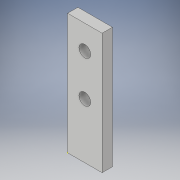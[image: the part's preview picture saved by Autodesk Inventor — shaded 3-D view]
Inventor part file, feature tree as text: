
AUTODESK INVENTOR PART (.ipt)
format: ipt  version: 2017 (Build 210142000, 142)  size: 104,960 bytes
history: native  units: in
note: dims shown in document units (in); Inventor stores cm internally (conversion verified against a paired STEP export)
features: sketch x4, extrude x1, hole x1
ambient origin geometry x8: Origin, YZ Plane, XZ Plane, XY Plane, X Axis, Y Axis, Z Axis, Center Point
bodies: Solid1 (feature_tree)
feature tree (6):
  extrude  "Extrusion1"  Depth=1.378in
  hole  "Hole1"  [1 undecoded]
  sketch  "Sketch3"  dims[d5=0.1969in]
  sketch  "Sketch4"  dims[d6=0.4724in d7=0.1969in d8=0.1339in d9=0.2362in d10=0.1575in d11=0.0787in d12=90.0deg d13=0.315in d14=0.8108in]
  sketch  "Sketch1"  dims[d0=0.3937in d1=1.378in]
  sketch  "Sketch2"  dims[d2=0.1181in d3=0.0in d4=0.2756in]
note: 1 required parameter value undecoded (feature->parameter linkage not recoverable at this tier; creation-order binding heuristic only, values carry confidence <= 0.55)
